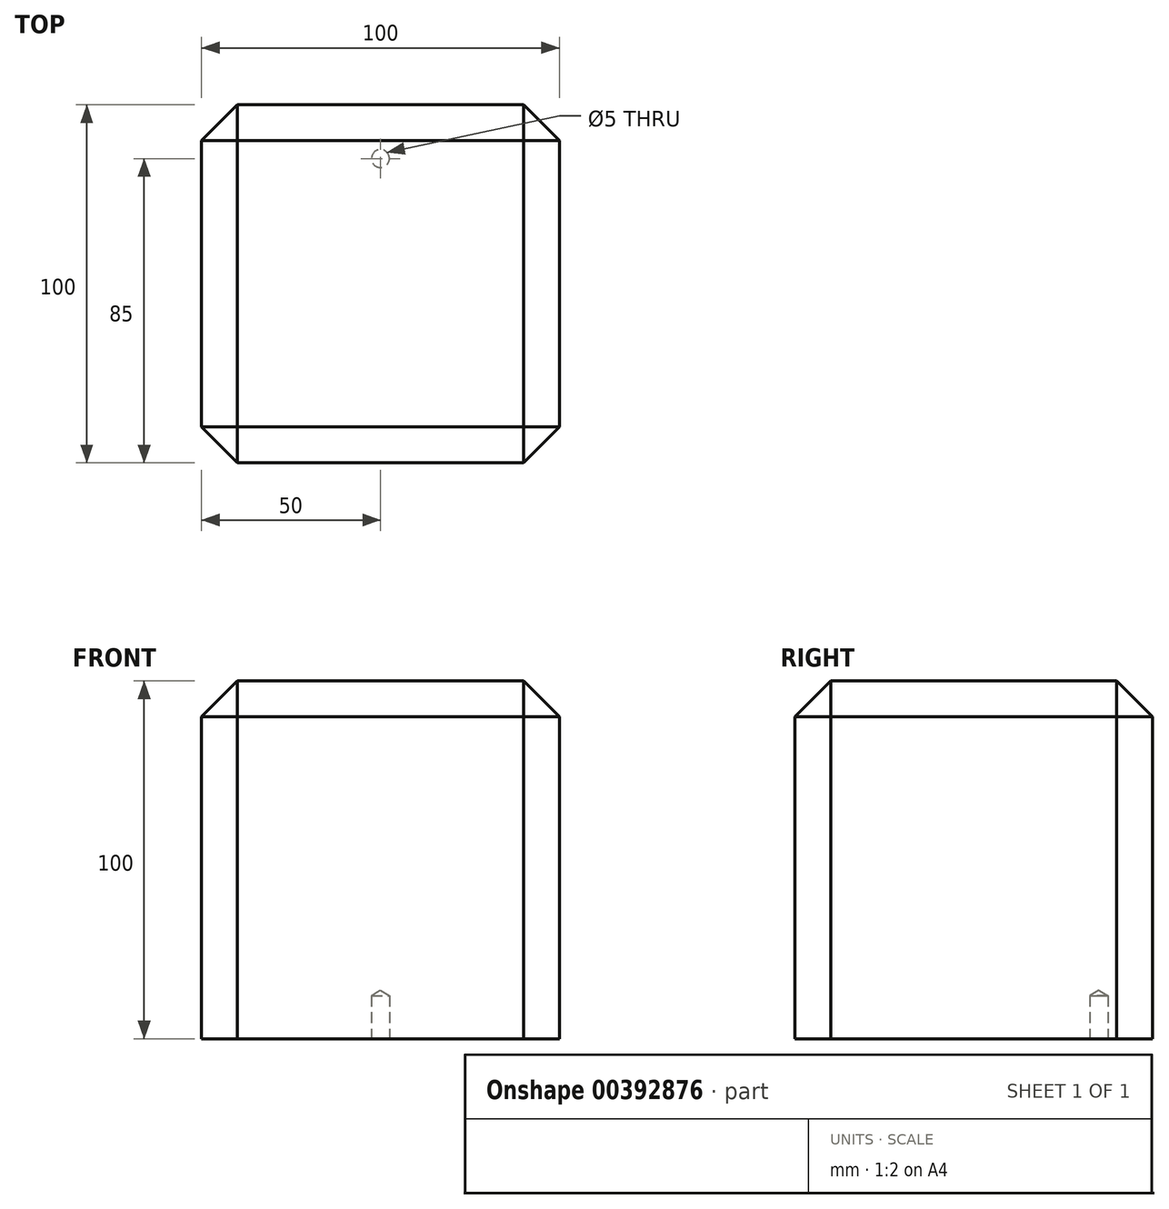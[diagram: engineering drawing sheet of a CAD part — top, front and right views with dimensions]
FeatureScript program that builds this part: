
annotation { "Feature Type Name" : "Feature", "Feature Type Description" : "" }
export const myFeature = defineFeature(function(context is Context, id is Id, definition is map)
    precondition{}
    {
        {
            var Q0;
            Q0=qCreatedBy(makeId("Front.planeOp"),FACE);
            var sketch = newSketch(context, id + "F0", { "sketchPlane" : qUnion([Q0])});
            skLineSegment(sketch, "E0.bottom", {"start": v(-50, 50) * mm, "end": v(50, 50) * mm});
            skLineSegment(sketch, "E0.top", {"start": v(-50, -50) * mm, "end": v(50, -50) * mm});
            skLineSegment(sketch, "E0.left", {"start": v(-50, 50) * mm, "end": v(-50, -50) * mm});
            skLineSegment(sketch, "E0.right", {"start": v(50, 50) * mm, "end": v(50, -50) * mm});
            skSolve(sketch);
        }
        {
            var Q0;
            Q0=makeQuery(id+"F0.imprint","IMPRINT",FACE,{"disambiguationData":[TD([[makeQuery(id+"F0.imprint","IMPRINT",EDGE,{"derivedFrom":sQuery(id+"F0.wireOp",EDGE,"E0.bottom")}),-1.0]])]});
            extrude(context, id + "F1", {"entities" : qUnion([Q0]), "endBound" : BoundingType.SYMMETRIC, "depth" : 100 * mm});
        }
        {
            var Q0;
            Q0=makeQuery(id+"F1.opExtrude","SWEPT_EDGE",EDGE,{"disambiguationData":[OSD([sQuery(id+"F0.wireOp",EDGE,"E0.bottom"),sQuery(id+"F0.wireOp",EDGE,"E0.left")])]});
            var Q1;
            Q1=makeQuery(id+"F1.opExtrude","CAP_EDGE",EDGE,{"disambiguationData":[OSD([sQuery(id+"F0.wireOp",EDGE,"E0.bottom")])],"isStart":false});
            var Q2;
            Q2=makeQuery(id+"F1.opExtrude","SWEPT_EDGE",EDGE,{"disambiguationData":[OSD([sQuery(id+"F0.wireOp",EDGE,"E0.bottom"),sQuery(id+"F0.wireOp",EDGE,"E0.right")])]});
            var Q3;
            Q3=makeQuery(id+"F1.opExtrude","CAP_EDGE",EDGE,{"disambiguationData":[OSD([sQuery(id+"F0.wireOp",EDGE,"E0.bottom")])],"isStart":true});
            var Q4;
            Q4=makeQuery(id+"F1.opExtrude","CAP_EDGE",EDGE,{"disambiguationData":[OSD([sQuery(id+"F0.wireOp",EDGE,"E0.right")])],"isStart":false});
            var Q5;
            Q5=makeQuery(id+"F1.opExtrude","CAP_EDGE",EDGE,{"disambiguationData":[OSD([sQuery(id+"F0.wireOp",EDGE,"E0.right")])],"isStart":true});
            var Q6;
            Q6=makeQuery(id+"F1.opExtrude","CAP_EDGE",EDGE,{"disambiguationData":[OSD([sQuery(id+"F0.wireOp",EDGE,"E0.left")])],"isStart":true});
            var Q7;
            Q7=makeQuery(id+"F1.opExtrude","CAP_EDGE",EDGE,{"disambiguationData":[OSD([sQuery(id+"F0.wireOp",EDGE,"E0.left")])],"isStart":false});
            chamfer(context, id + "F2", {"entities" : qUnion([Q0, Q1, Q2, Q3, Q4, Q5, Q6, Q7]), "width" : 10 * mm, "tangentPropagation" : true});
        }
        {
            var Q0;
            Q0=makeQuery(id+"F1.opExtrude","SWEPT_FACE",FACE,{"disambiguationData":[OSD([sQuery(id+"F0.wireOp",EDGE,"E0.top")])]});
            var sketch = newSketch(context, id + "F3", { "sketchPlane" : qUnion([Q0])});
            skPoint(sketch, "E1", {"position": v(0, -35) * mm});
            skPoint(sketch, "E2", {"position": v(-24.44, 28.25) * mm});
            skSolve(sketch);
        }
        {
            var Q0;
            Q0=sQuery(id+"F3.wireOp",VERTEX,"E1");
            var Q1;
            Q1=makeQuery(id+"F1.opExtrude","SWEPT_BODY",BODY,{"disambiguationData":[OSD([sQuery(id+"F0.wireOp",EDGE,"E0.bottom"),sQuery(id+"F0.wireOp",EDGE,"E0.top"),sQuery(id+"F0.wireOp",EDGE,"E0.left"),sQuery(id+"F0.wireOp",EDGE,"E0.right")])]});
            hole(context, id + "F4", {"style" : HoleStyle.SIMPLE, "endStyle" : HoleEndStyle.BLIND, "standardTappedOrClearance" : lookupTablePath({ "fit" : "Normal", "standard" : "ISO", "size" : "5", "type" : "Drilled" }), "standardBlindInLast" : lookupTablePath({ "fit" : "Standard", "standard" : "ISO", "size" : "5", "type" : "Drilled" }), "holeDiameter" : 5 * mm, "holeDepth" : 12 * mm, "isTappedThrough" : true, "tappedDepth" : 12 * mm, "tapClearance" : 3, "locations" : qUnion([Q0]), "scope" : qUnion([Q1])});
        }
    });
